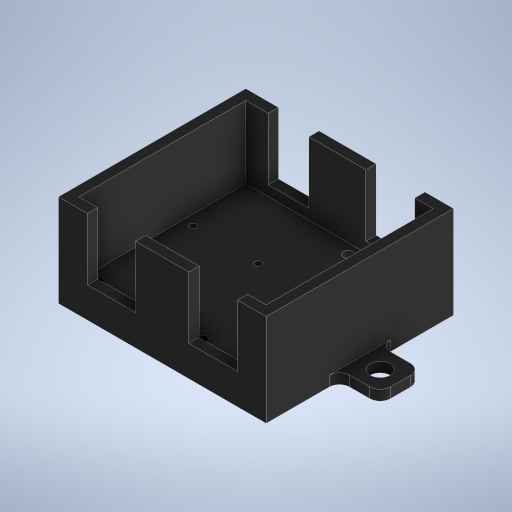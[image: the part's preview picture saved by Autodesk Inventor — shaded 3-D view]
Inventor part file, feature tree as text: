
AUTODESK INVENTOR PART (.ipt)
format: ipt  version: 2024 (Build 280153000, 153)  size: 603,136 bytes
history: native  units: in
note: dims shown in document units (in); Inventor stores cm internally (conversion verified against a paired STEP export)
features: projected_geometry x8, extrude x5, sketch x5, fillet x1
ambient origin geometry x8: Origin, YZ Plane, XZ Plane, XY Plane, X Axis, Y Axis, Z Axis, Center Point
bodies: Solid1 (feature_tree)
feature tree (19):
  extrude  "Extrusion1"  Depth=0.125in TaperAngle=0.0deg
  extrude  "Extrusion2"  Depth=0.125in
  extrude  "Extrusion3"  Depth=0.76in TaperAngle=0.0deg
  extrude  "Extrusion4"  Depth=0.125in
  sketch  "Sketch6"  dims[d9=0.125in d10=0.0in d11=0.22in]
  extrude  "Extrusion5"  Depth=0.125in
  fillet  "Fillet1"  Radius=0.11in
  sketch  "Sketch3"  dims[d0=0.25in d1=0.125in d2=0.0in]
  sketch  "Sketch4"  dims[d3=0.025in d4=0.125in]
  projected_geometry  "Projected Loop1"
  projected_geometry  "Projected Loop2"
  projected_geometry  "Projected Loop3"
  sketch  "Sketch5"  dims[d5=0.125in d6=0.0in d7=0.76in d8=0.0in]
  projected_geometry  "Projected Loop4"
  projected_geometry  "Projected Loop5"
  projected_geometry  "Projected Loop6"
  projected_geometry  "Projected Loop7"
  sketch  "Sketch7"  dims[d12=0.22in d13=0.22in d14=0.11in d15=0.22in d16=0.125in d17=0.5in d18=0.25in d19=0.5in d20=0.5in d21=0.5in d22=0.25in d23=0.25in d24=0.125in d25=0.125in d26=0.0in d27=0.125in]
  projected_geometry  "Projected Loop8"
